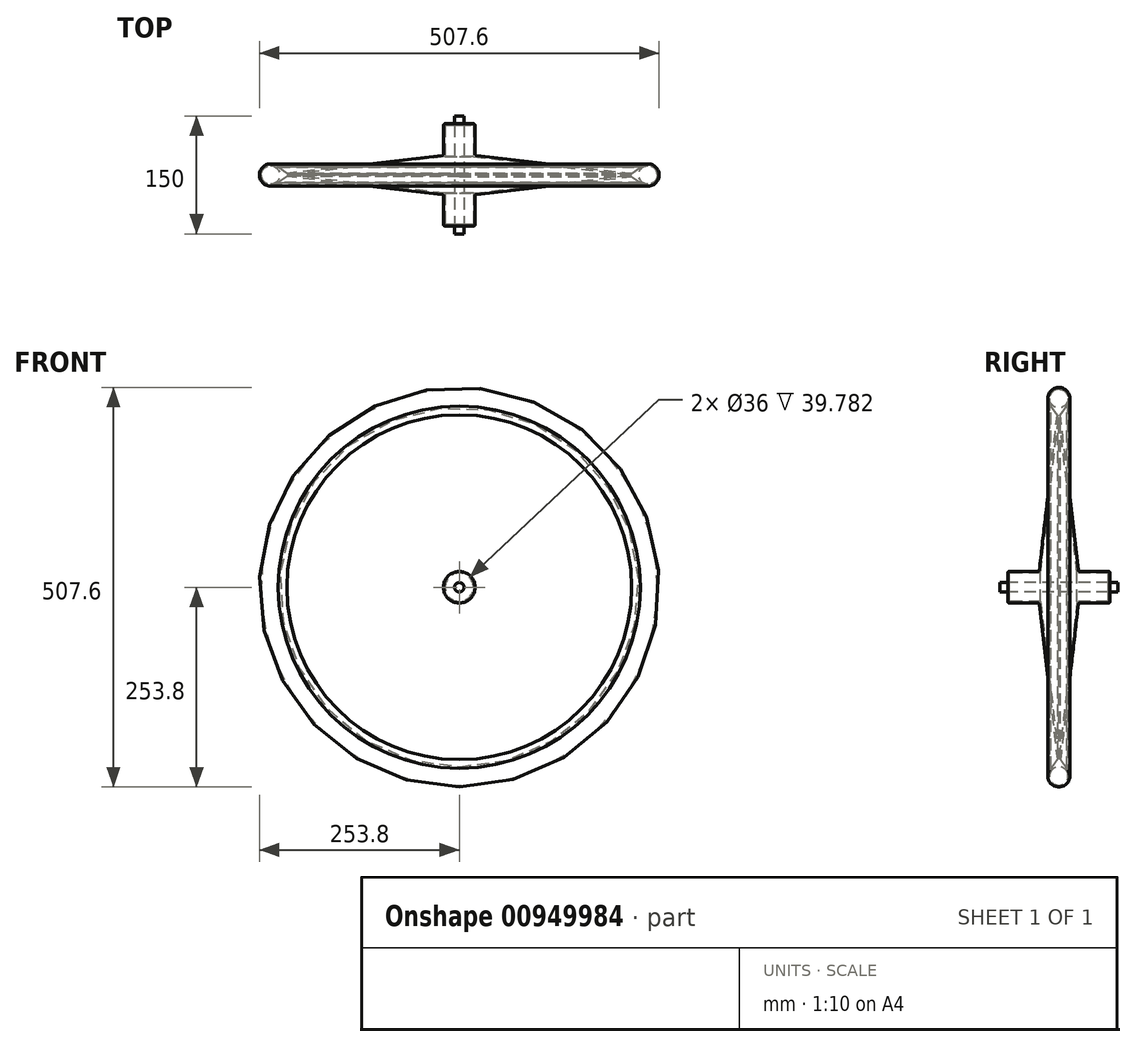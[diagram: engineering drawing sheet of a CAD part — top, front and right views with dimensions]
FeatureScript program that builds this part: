
annotation { "Feature Type Name" : "Feature", "Feature Type Description" : "" }
export const myFeature = defineFeature(function(context is Context, id is Id, definition is map)
    precondition{}
    {
        {
            var Q0;
            Q0=qCreatedBy(makeId("Right.planeOp"),FACE);
            var sketch = newSketch(context, id + "F0", { "sketchPlane" : qUnion([Q0])});
            skLineSegment(sketch, "E0", {"start": v(-75, 0) * mm, "end": v(-75, -6) * mm});
            skLineSegment(sketch, "E1", {"start": v(-75, -6) * mm, "end": v(-65, -6) * mm});
            skLineSegment(sketch, "E2", {"start": v(-65, -6) * mm, "end": v(-65, -20) * mm});
            skLineSegment(sketch, "E3", {"start": v(-65, -20) * mm, "end": v(-25, -20) * mm});
            skLineSegment(sketch, "E4", {"start": v(-25, -20) * mm, "end": v(-2, -219) * mm});
            skLineSegment(sketch, "E5", {"start": v(0, 28.17) * mm, "end": v(0, -136.08) * mm, "construction": true});
            skLineSegment(sketch, "E6", {"start": v(0, -136.08) * mm, "end": v(0, -310.94) * mm, "construction": true});
            skLineSegment(sketch, "E7", {"start": v(-75, 0) * mm, "end": v(0, 0) * mm});
            skLineSegment(sketch, "E8", {"start": v(-2, -219) * mm, "end": v(-10, -230) * mm});
            skArc(sketch, "E9", {"start": v(-10, -230) * mm, "mid": v(-12.9, -245.22) * mm, "end": v(0, -253.8) * mm});
            skPoint(sketch, "E9.first.point", {"position": v(10, -230) * mm});
            skPoint(sketch, "E9.second.point", {"position": v(0, -253.8) * mm});
            skPoint(sketch, "E10", {"position": v(-141.28, -165.37) * mm});
            skPoint(sketch, "E11", {"position": v(0, -225.8) * mm});
            skLineSegment(sketch, "E12", {"start": v(0, 74.18) * mm, "end": v(0, -390.4) * mm, "construction": true});
            skLineSegment(sketch, "E13.MirrorCS", {"start": v(75, 0) * mm, "end": v(75, -6) * mm});
            skLineSegment(sketch, "E14.MirrorCS", {"start": v(75, -6) * mm, "end": v(65, -6) * mm});
            skLineSegment(sketch, "E15.MirrorCS", {"start": v(65, -6) * mm, "end": v(65, -20) * mm});
            skLineSegment(sketch, "E16.MirrorCS", {"start": v(25, -20) * mm, "end": v(2, -219) * mm});
            skLineSegment(sketch, "E17.MirrorCS", {"start": v(2, -219) * mm, "end": v(10, -230) * mm});
            skArc(sketch, "E18.MirrorCS", {"start": v(10, -230) * mm, "mid": v(12.9, -245.22) * mm, "end": v(0, -253.8) * mm});
            skLineSegment(sketch, "E19.MirrorCS", {"start": v(65, -20) * mm, "end": v(25, -20) * mm});
            skLineSegment(sketch, "E20.MirrorCS", {"start": v(75, 0) * mm, "end": v(0, 0) * mm});
            skLineSegment(sketch, "E21", {"start": v(-63, -6) * mm, "end": v(63, -6) * mm});
            skLineSegment(sketch, "E22", {"start": v(63, -6) * mm, "end": v(63, -18) * mm});
            skLineSegment(sketch, "E23", {"start": v(63, -18) * mm, "end": v(23.22, -18) * mm});
            skLineSegment(sketch, "E24", {"start": v(23.22, -18) * mm, "end": v(0, -218.88) * mm});
            skLineSegment(sketch, "E25", {"start": v(0, -218.88) * mm, "end": v(-23.22, -18) * mm});
            skLineSegment(sketch, "E26", {"start": v(-23.22, -18) * mm, "end": v(-63, -18) * mm});
            skLineSegment(sketch, "E27", {"start": v(-63, -18) * mm, "end": v(-63, -6) * mm});
            skCircle(sketch, "E28", {"center": v(0, -239.8) * mm, "radius": 11.8 * mm});
            skSolve(sketch);
        }
        {
            var Q0;
            Q0=makeQuery(id+"F0.imprint","IMPRINT",FACE,{"disambiguationData":[TD([[makeQuery(id+"F0.imprint","IMPRINT",EDGE,{"derivedFrom":sQuery(id+"F0.wireOp",EDGE,"E0")}),1.0]])]});
            var Q1;
            Q1=sQuery(id+"F0.wireOp",EDGE,"E7");
            revolve(context, id + "F1", {"surfaceOperationType" : NewSurfaceOperationType.NEW, "entities" : qUnion([Q0]), "axis" : qUnion([Q1]), "revolveType" : RevolveType.FULL});
        }
        {
            var Q0;
            Q0=makeQuery(id+"F1.opRevolve","SWEPT_EDGE",EDGE,{"disambiguationData":[OSD([sQuery(id+"F0.wireOp",EDGE,"E2"),sQuery(id+"F0.wireOp",EDGE,"E3")])]});
            var Q1;
            Q1=makeQuery(id+"F1.opRevolve","SWEPT_EDGE",EDGE,{"disambiguationData":[OSD([sQuery(id+"F0.wireOp",EDGE,"E3"),sQuery(id+"F0.wireOp",EDGE,"E4")])]});
            var Q2;
            Q2=makeQuery(id+"F1.opRevolve","SWEPT_EDGE",EDGE,{"disambiguationData":[OSD([sQuery(id+"F0.wireOp",EDGE,"E19.MirrorCS"),sQuery(id+"F0.wireOp",EDGE,"E16.MirrorCS")])]});
            var Q3;
            Q3=makeQuery(id+"F1.opRevolve","SWEPT_EDGE",EDGE,{"disambiguationData":[OSD([sQuery(id+"F0.wireOp",EDGE,"E15.MirrorCS"),sQuery(id+"F0.wireOp",EDGE,"E19.MirrorCS")])]});
            fillet(context, id + "F2", {"entities" : qUnion([Q0, Q1, Q2, Q3]), "tangentPropagation" : true, "radius" : 2 * mm, "defaultsChanged" : false, "vertexSettings" : [], "allowEdgeOverflow" : false});
        }
    });
